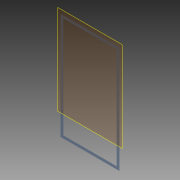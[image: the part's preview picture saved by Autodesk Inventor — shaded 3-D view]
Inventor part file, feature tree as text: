
AUTODESK INVENTOR PART (.ipt)
format: ipt  version: 2013 (Build 170138000, 138)  size: 74,240 bytes
history: native  units: in
note: dims shown in document units (in); Inventor stores cm internally (conversion verified against a paired STEP export)
features: plane x1, extrude x1, sketch x1
ambient origin geometry x8: Origin, YZ Plane, XZ Plane, XY Plane, X Axis, Y Axis, Z Axis, Center Point
bodies: Solid1 (feature_tree)
feature tree (3):
  plane  "Work Plane1"
  extrude  "Extrusion1"  [1 undecoded]
  sketch  "Sketch1"  dims[d1=0.001in d2=0.0in]
note: 1 required parameter value undecoded (feature->parameter linkage not recoverable at this tier; creation-order binding heuristic only, values carry confidence <= 0.55)
